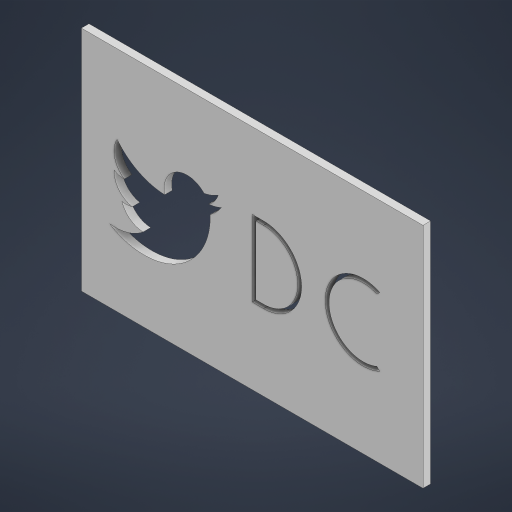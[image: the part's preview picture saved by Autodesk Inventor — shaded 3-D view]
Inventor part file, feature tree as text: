
AUTODESK INVENTOR PART (.ipt)
format: ipt  version: 2023.4 (Build 274418000, 418)  size: 254,976 bytes
history: native  units: mm
features: extrude x2, sketch x2, other x1
ambient origin geometry x8: Origin, YZ Plane, XZ Plane, XY Plane, X Axis, Y Axis, Z Axis, Center Point
bodies: Body1 (feature_tree)
feature tree (5):
  extrude  "Extrusion3"  Depth=300.0mm
  extrude  "Extrusion4"  Depth=100.0mm
  sketch  "Sketch3"  dims[d28=450.0mm d29=300.0mm]
  sketch  "Sketch4"  dims[d30=10.0mm d31=0.0mm d33=100.0mm d36=50.0mm d37=15.0mm d38=15.0mm d39=5.0mm d41=5.0mm d42=45.0deg d45=0.0mm d46=0.0mm]
  other  "Image2"
